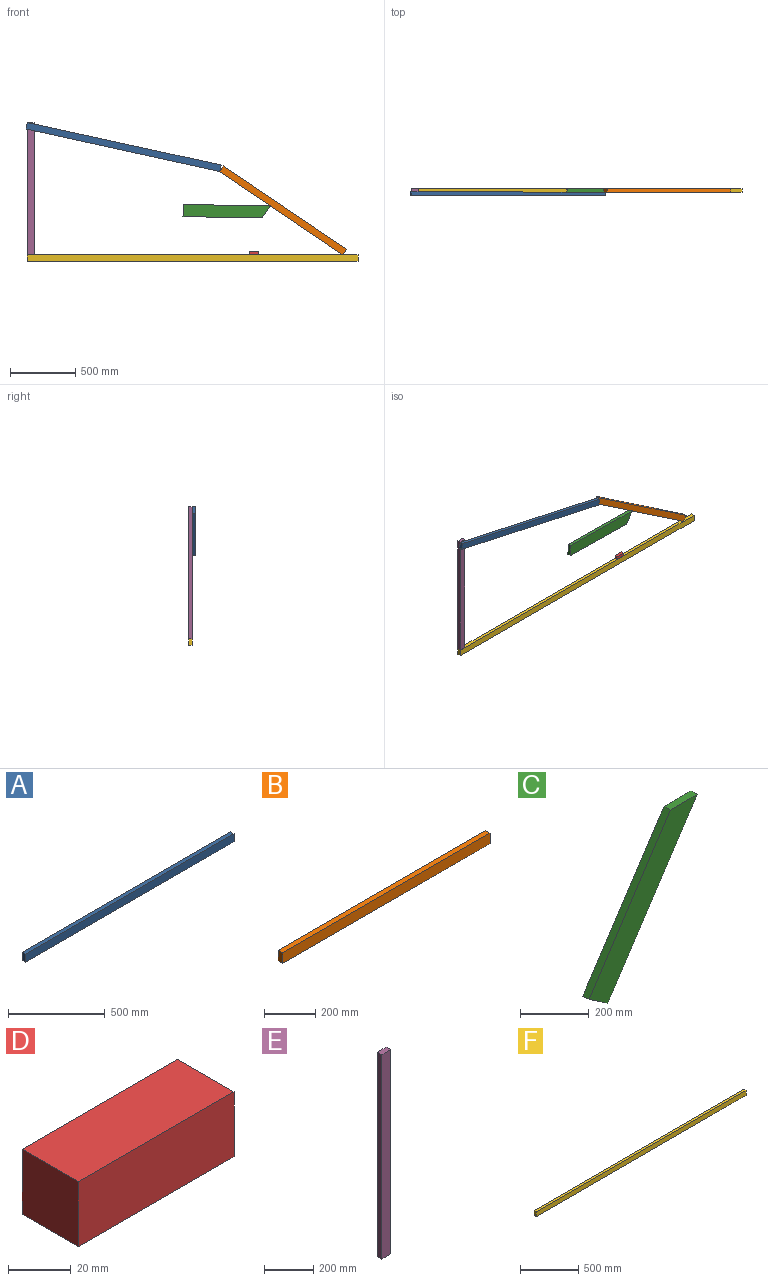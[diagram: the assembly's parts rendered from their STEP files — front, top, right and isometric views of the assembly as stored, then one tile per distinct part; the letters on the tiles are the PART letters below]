
ASSEMBLY  parts=6 mates=5
PART A: 6 faces, bbox 1524x25.4x50.8 mm
  f0: plane 1524x25.4mm, normal (0,0,1), area 38709.6mm2, adj f1,f3,f4,f5
  f1: plane 50.8x25.4mm, normal (-1,0,0), area 1290.3mm2, adj f0,f2,f4,f5
  f2: plane 1524x25.4mm, normal (0,0,-1), area 38709.6mm2, adj f1,f3,f4,f5
  f3: plane 50.8x25.4mm, normal (1,0,0), area 1290.3mm2, adj f0,f2,f4,f5
  f4: plane 1524x50.8mm, normal (0,-1,0), area 77419.2mm2, adj f0,f1,f2,f3
  f5: plane 1524x50.8mm, normal (0,1,0), area 77419.2mm2, adj f0,f1,f2,f3
PART B: 6 faces, bbox 1143x25.4x50.8 mm
  f0: plane 1143x25.4mm, normal (0,0,1), area 29032.2mm2, adj f1,f3,f4,f5
  f1: plane 50.8x25.4mm, normal (-1,0,0), area 1290.3mm2, adj f0,f2,f4,f5
  f2: plane 1143x25.4mm, normal (0,0,-1), area 29032.2mm2, adj f1,f3,f4,f5
  f3: plane 50.8x25.4mm, normal (1,0,0), area 1290.3mm2, adj f0,f2,f4,f5
  f4: plane 1143x50.8mm, normal (0,-1,0), area 58064.4mm2, adj f0,f1,f2,f3
  f5: plane 1143x50.8mm, normal (0,1,0), area 58064.4mm2, adj f0,f1,f2,f3
PART C: 6 faces, bbox 446x25.4x560.3 mm
  f0: plane 509.23x334.73mm, normal (-0.84,0,0.55), area 15478.5mm2, adj f1,f2,f4,f5
  f1: plane 560.32x446.05mm, normal (0,-1,0), area 59528.8mm2, adj f0,f3,f4,f5
  f2: plane 560.32x446.05mm, normal (0,1,0), area 59528.8mm2, adj f0,f3,f4,f5
  f3: plane 560.32x368.31mm, normal (0.84,0,-0.55), area 17031.5mm2, adj f1,f2,f4,f5
  f4: plane 111.32x25.4mm, normal (0,0,1), area 2827.4mm2, adj f0,f1,f2,f3
  f5: plane 77.73x51.09mm, normal (-0.55,0,-0.84), area 2362.7mm2, adj f0,f1,f2,f3
PART D: 6 faces, bbox 70.3x25.4x25.4 mm
  f0: plane 70.32x25.4mm, normal (0,-1,0), area 1786mm2, adj f1,f3,f4,f5
  f1: plane 25.4x25.4mm, normal (1,0,0), area 645.2mm2, adj f0,f2,f4,f5
  f2: plane 70.32x25.4mm, normal (0,1,0), area 1786mm2, adj f1,f3,f4,f5
  f3: plane 25.4x25.4mm, normal (-1,0,0), area 645.2mm2, adj f0,f2,f4,f5
  f4: plane 70.32x25.4mm, normal (0,0,1), area 1786mm2, adj f0,f1,f2,f3
  f5: plane 70.32x25.4mm, normal (0,0,-1), area 1786mm2, adj f0,f1,f2,f3
PART E: 6 faces, bbox 50.8x25.4x1016 mm
  f0: plane 1016x25.4mm, normal (-1,0,0), area 25806.4mm2, adj f1,f3,f4,f5
  f1: plane 50.8x25.4mm, normal (0,0,-1), area 1290.3mm2, adj f0,f2,f4,f5
  f2: plane 1016x25.4mm, normal (1,0,0), area 25806.4mm2, adj f1,f3,f4,f5
  f3: plane 50.8x25.4mm, normal (0,0,1), area 1290.3mm2, adj f0,f2,f4,f5
  f4: plane 1016x50.8mm, normal (0,-1,0), area 51612.8mm2, adj f0,f1,f2,f3
  f5: plane 1016x50.8mm, normal (0,1,0), area 51612.8mm2, adj f0,f1,f2,f3
PART F: 6 faces, bbox 2540x25.4x50.8 mm
  f0: plane 2540x25.4mm, normal (0,0,1), area 64516mm2, adj f1,f3,f4,f5
  f1: plane 50.8x25.4mm, normal (-1,0,0), area 1290.3mm2, adj f0,f2,f4,f5
  f2: plane 2540x25.4mm, normal (0,0,-1), area 64516mm2, adj f1,f3,f4,f5
  f3: plane 50.8x25.4mm, normal (1,0,0), area 1290.3mm2, adj f0,f2,f4,f5
  f4: plane 2540x50.8mm, normal (0,-1,0), area 129032mm2, adj f0,f1,f2,f3
  f5: plane 2540x50.8mm, normal (0,1,0), area 129032mm2, adj f0,f1,f2,f3
PLACE A rot(axis=(0,1,0),12.4deg) t=(-242.79,25.4,23.53)mm
PLACE B rot(axis=(0,1,0),34.1deg) t=(-350.69,76.2,694.47)mm
PLACE C rot(axis=(0.88,0,0.47),180deg) t=(-166.05,-76.2,-778.18)mm
PLACE D t=(-170.19,50.8,-50.8)mm
PLACE E t=(-25.4,25.4,0)mm
PLACE F t=(-25.4,50.8,-50.8)mm
MATE fastened D.f5 <-> F.f0  axis (0,0,-1) through (1752.6,0,0)mm
MATE fastened F.f0 <-> E.f1  axis (0,0,1) through (-25.4,0,0)mm
MATE revolute E.f4 <-> A.f5  axis (0,-1,0) through (-25.4,0,1016)mm
MATE fastened C.f2 <-> B.f4  axis (0,-1,0) through (1841.69,0,377.06)mm
MATE revolute B.f4 <-> A.f5  axis (0,-1,0) through (1452.44,0,640.29)mm
